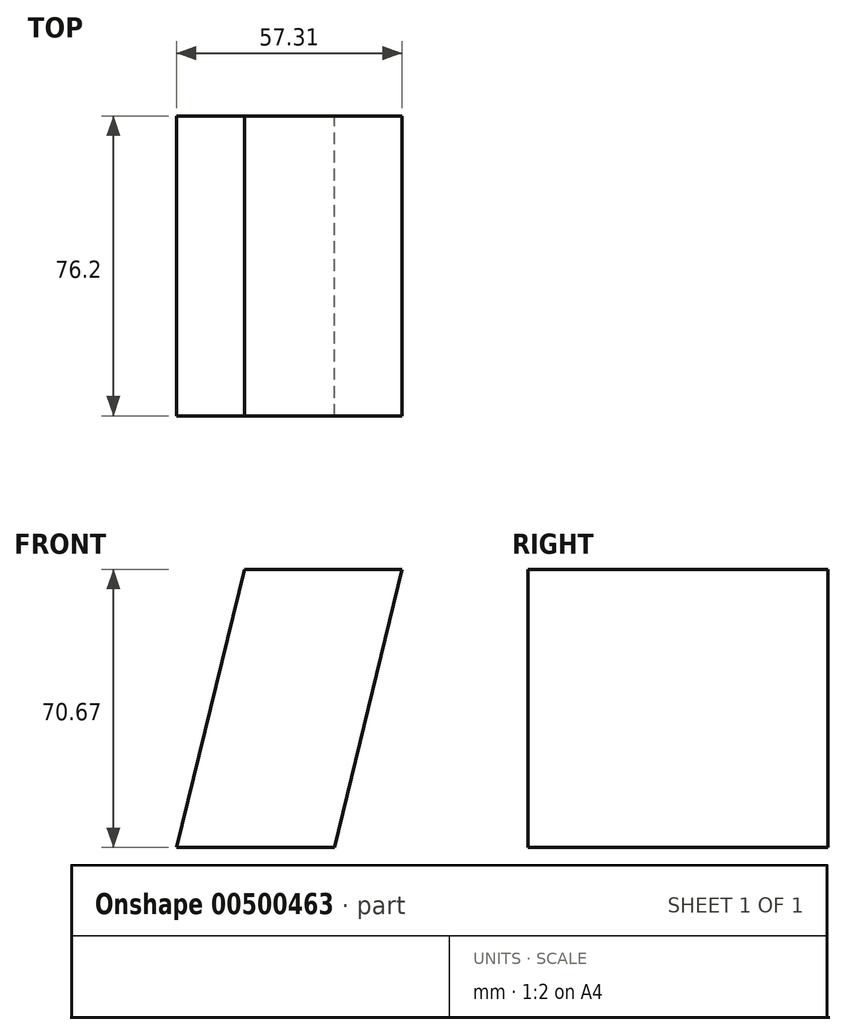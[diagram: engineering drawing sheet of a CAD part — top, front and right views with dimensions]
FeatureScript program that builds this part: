
annotation { "Feature Type Name" : "Feature", "Feature Type Description" : "" }
export const myFeature = defineFeature(function(context is Context, id is Id, definition is map)
    precondition{}
    {
        {
            var Q0;
            Q0=qCreatedBy(makeId("Front.planeOp"),FACE);
            var sketch = newSketch(context, id + "F0", { "sketchPlane" : qUnion([Q0])});
            skLineSegment(sketch, "E0", {"start": v(-56.88, 34.52) * mm, "end": v(-16.87, 34.52) * mm});
            skLineSegment(sketch, "E1", {"start": v(-16.87, 35.41) * mm, "end": v(-20.9, 34.52) * mm});
            skLineSegment(sketch, "E2", {"start": v(-16.87, 34.52) * mm, "end": v(-34.01, -36.15) * mm});
            skLineSegment(sketch, "E3", {"start": v(-74.18, -36.15) * mm, "end": v(-34.01, -36.15) * mm});
            skLineSegment(sketch, "E4", {"start": v(-74.18, -36.15) * mm, "end": v(-56.88, 34.52) * mm});
            skSolve(sketch);
        }
        {
            var Q0;
            {var subQ0=sQuery(id+"F0.wireOp",EDGE,"E2");Q0=makeQuery(id+"F0.imprint","IMPRINT",FACE,{"disambiguationData":[TD([[makeQuery(id+"F0.imprint","IMPRINT",EDGE,{"derivedFrom":subQ0}),-1.0]])]});}
            extrude(context, id + "F1", {"entities" : qUnion([Q0]), "depth" : 76.2 * mm, "offsetDistance" : 25.4 * mm});
        }
    });
